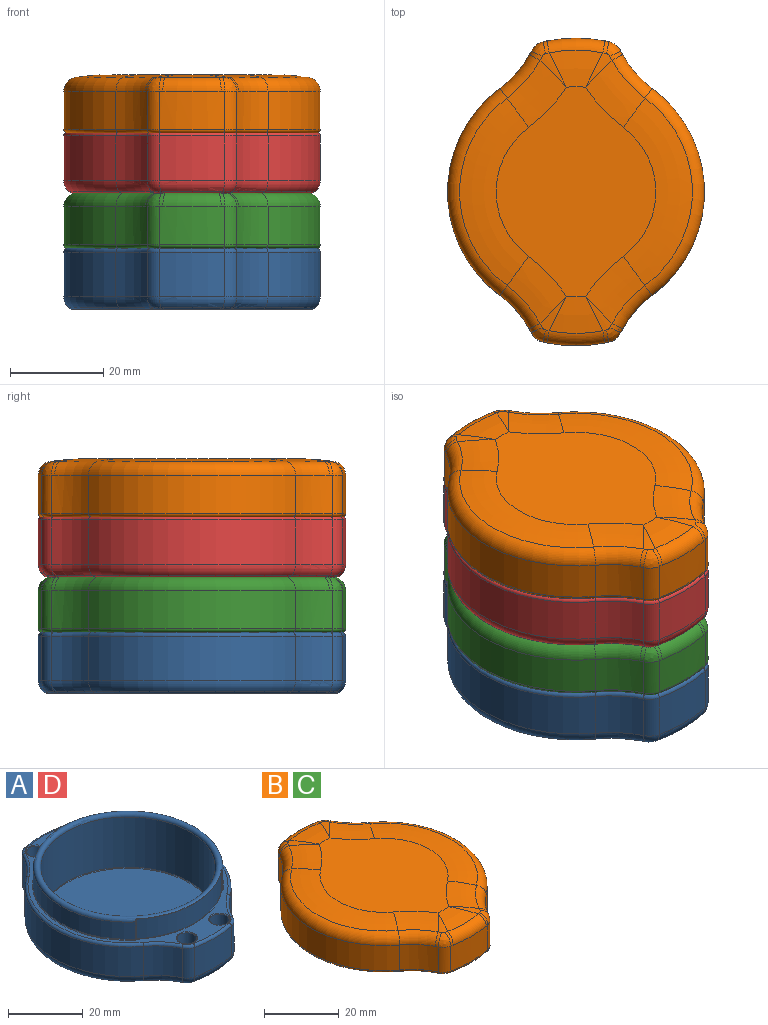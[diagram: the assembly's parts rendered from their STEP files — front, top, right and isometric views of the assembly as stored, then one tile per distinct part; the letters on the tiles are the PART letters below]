
ASSEMBLY  parts=4 mates=1
PART A: 130 faces, bbox 59.6x71.3x20.3 mm
  f0: cylinder r=25.3mm len=38.57mm, axis (0,0,-1), area 245.6mm2, adj f2,f60,f103,f117
  f1: torus R=25.5mm, axis (0,0,-1), area 13.8mm2, adj f3,f6,f114,f129
  f2: torus R=25.5mm, axis (0,0,-1), area 13.8mm2, adj f0,f3,f101,f115
  f3: plane 64.31x53.51mm, normal (0,0,1), area 354.2mm2, adj f1,f2,f39,f40,f41,f42,f43,f44
  f4: cylinder r=27.5mm len=44.33mm, axis (0,0,-1), area 494.9mm2, adj f23,f26,f37,f50
  f5: cylinder r=23.3mm len=46.6mm, axis (0,0,-1), area 2400.9mm2, adj f59,f60
  f6: cylinder r=25.3mm len=38.57mm, axis (0,0,-1), area 245.6mm2, adj f1,f60,f113,f128
  f7: cylinder r=27.5mm len=44.33mm, axis (0,0,-1), area 494.9mm2, adj f24,f25,f28,f39
  f8: plane 46.2x46.2mm, normal (0,0,1), area 1676.4mm2, adj f59
  f9: cylinder r=3.9mm len=9.6mm, axis (0,0,1), area 33.5mm2, adj f10,f25,f32,f42
  f10: cylinder r=32.9mm len=13.89mm, axis (0,0,1), area 134.3mm2, adj f9,f11,f34,f44
  f11: cylinder r=3.9mm len=9.6mm, axis (0,0,1), area 33.5mm2, adj f10,f26,f36,f46
  f12: cylinder r=3.9mm len=9.6mm, axis (0,0,1), area 33.5mm2, adj f13,f23,f33,f47
  f13: cylinder r=32.9mm len=13.89mm, axis (0,0,1), area 134.3mm2, adj f12,f14,f31,f45
  f14: cylinder r=3.9mm len=9.6mm, axis (0,0,1), area 33.5mm2, adj f13,f24,f29,f43
  f15: cylinder r=2.65mm len=11.8mm, axis (0,0,1), area 196.5mm2, adj f57,f58
  f16: plane 4.9x4.9mm, normal (0,0,1), area 18.9mm2, adj f58
  f17: cylinder r=2.65mm len=11.8mm, axis (0,0,1), area 196.5mm2, adj f55,f56
  f18: plane 4.9x4.9mm, normal (0,0,1), area 18.9mm2, adj f56
  f19: cylinder r=2.65mm len=11.8mm, axis (0,0,1), area 196.5mm2, adj f53,f54
  f20: plane 4.9x4.9mm, normal (0,0,1), area 18.9mm2, adj f54
  f21: cylinder r=2.65mm len=11.8mm, axis (0,0,1), area 196.5mm2, adj f51,f52
  f22: plane 4.9x4.9mm, normal (0,0,1), area 18.9mm2, adj f52
  f23: cylinder r=22mm len=9.6mm, axis (0,0,-1), area 100.4mm2, adj f4,f12,f35,f49
  f24: cylinder r=22mm len=9.6mm, axis (0,0,1), area 100.4mm2, adj f7,f14,f27,f41
  f25: cylinder r=22mm len=9.6mm, axis (0,0,-1), area 100.4mm2, adj f7,f9,f30,f40
  f26: cylinder r=22mm len=9.6mm, axis (0,0,1), area 100.4mm2, adj f4,f11,f38,f48
  f27: torus R=25mm, axis (0,0,-1), area 28.2mm2, adj f24,f28,f29,f91,f93
  f28: torus R=24.5mm, axis (0,0,-1), area 134.7mm2, adj f7,f27,f30,f92
  f29: torus R=0.9mm, axis (0,0,-1), area 8.5mm2, adj f14,f27,f31,f89
  f30: torus R=25mm, axis (0,0,-1), area 28.2mm2, adj f25,f28,f32,f88,f90
  f31: torus R=29.9mm, axis (0,0,-1), area 36.6mm2, adj f13,f29,f33,f83,f85,f87
  f32: torus R=0.9mm, axis (0,0,-1), area 8.5mm2, adj f9,f30,f34,f86
  f33: torus R=0.9mm, axis (0,0,-1), area 8.5mm2, adj f12,f31,f35,f81
  f34: torus R=29.9mm, axis (0,0,-1), area 36.6mm2, adj f10,f32,f36,f80,f82,f84
  f35: torus R=25mm, axis (0,0,-1), area 28.2mm2, adj f23,f33,f37,f77,f79
  f36: torus R=0.9mm, axis (0,0,-1), area 8.5mm2, adj f11,f34,f38,f78
  f37: torus R=24.5mm, axis (0,0,-1), area 134.7mm2, adj f4,f35,f38,f75
  f38: torus R=25mm, axis (0,0,-1), area 28.2mm2, adj f26,f36,f37,f74,f76
  f39: torus R=26.7mm, axis (0,0,-1), area 64.1mm2, adj f3,f7,f40,f41
  f40: torus R=22.8mm, axis (0,0,-1), area 13.3mm2, adj f3,f25,f39,f42
  f41: torus R=22.8mm, axis (0,0,-1), area 13.3mm2, adj f3,f24,f39,f43
  f42: torus R=3.1mm, axis (0,0,-1), area 4.1mm2, adj f3,f9,f40,f44
  f43: torus R=3.1mm, axis (0,0,-1), area 4.1mm2, adj f3,f14,f41,f45
  f44: torus R=32.1mm, axis (0,0,-1), area 17.4mm2, adj f3,f10,f42,f46
  f45: torus R=32.1mm, axis (0,0,-1), area 17.4mm2, adj f3,f13,f43,f47
  f46: torus R=3.1mm, axis (0,0,-1), area 4.1mm2, adj f3,f11,f44,f48
  f47: torus R=3.1mm, axis (0,0,-1), area 4.1mm2, adj f3,f12,f45,f49
  f48: torus R=22.8mm, axis (0,0,-1), area 13.3mm2, adj f3,f26,f46,f50
  f49: torus R=22.8mm, axis (0,0,-1), area 13.3mm2, adj f3,f23,f47,f50
  f50: torus R=26.7mm, axis (0,0,-1), area 64.1mm2, adj f3,f4,f48,f49
  f51: torus R=2.85mm, axis (0,0,-1), area 5.4mm2, adj f3,f21
  f52: torus R=2.45mm, axis (0,0,-1), area 5.1mm2, adj f21,f22
  f53: torus R=2.85mm, axis (0,0,-1), area 5.4mm2, adj f3,f19
  f54: torus R=2.45mm, axis (0,0,-1), area 5.1mm2, adj f19,f20
  f55: torus R=2.85mm, axis (0,0,-1), area 5.4mm2, adj f3,f17
  f56: torus R=2.45mm, axis (0,0,-1), area 5.1mm2, adj f17,f18
  f57: torus R=2.85mm, axis (0,0,-1), area 5.4mm2, adj f3,f15
  f58: torus R=2.45mm, axis (0,0,-1), area 5.1mm2, adj f15,f16
  f59: torus R=23.1mm, axis (0,0,-1), area 45.8mm2, adj f5,f8
  f60: torus R=24.3mm, axis (0,0,-1), area 420.2mm2, adj f0,f5,f6,f106,f108,f110,f111,f112
  f61: plane 45.02x34.22mm, normal (0,0,-1), area 1021mm2, adj f62,f63,f64,f67,f68,f71,f72,f73
  f62: torus R=17.11mm, axis (0,0,1), area 327.2mm2, adj f61,f63,f64,f92
  f63: torus R=32.39mm, axis (0,0,-1), area 94mm2, adj f61,f62,f65,f93
  f64: torus R=32.39mm, axis (0,0,-1), area 94mm2, adj f61,f62,f66,f90
  f65: bspline ~9.74x7.58mm, area 12mm2, adj f63,f67,f87,f89,f91
  f66: bspline ~9.74x7.58mm, area 12mm2, adj f64,f68,f84,f86,f88
  f67: torus R=22.51mm, axis (0,0,1), area 63.5mm2, adj f61,f65,f69,f85
  f68: torus R=22.51mm, axis (0,0,1), area 63.5mm2, adj f61,f66,f70,f82
  f69: bspline ~9.74x7.58mm, area 12mm2, adj f67,f71,f79,f81,f83
  f70: bspline ~9.74x7.58mm, area 12mm2, adj f68,f72,f76,f78,f80
  f71: torus R=32.39mm, axis (0,0,-1), area 94mm2, adj f61,f69,f73,f77
  f72: torus R=32.39mm, axis (0,0,-1), area 94mm2, adj f61,f70,f73,f74
  f73: torus R=17.11mm, axis (0,0,1), area 327.2mm2, adj f61,f71,f72,f75
  f74: torus R=23.98mm, axis (0,0,-1), area 12.3mm2, adj f38,f72,f75,f76
  f75: torus R=25.52mm, axis (0,0,1), area 57mm2, adj f37,f73,f74,f77
  f76: bspline ~2.23x1.86mm, area 0.8mm2, adj f38,f70,f74,f78
  f77: torus R=23.98mm, axis (0,0,-1), area 12.3mm2, adj f35,f71,f75,f79
  f78: bspline ~2.64x2.48mm, area 2.4mm2, adj f36,f70,f76,f80
  f79: bspline ~2.23x1.86mm, area 0.8mm2, adj f35,f69,f77,f81
  f80: bspline ~1.64x1.37mm, area 0.7mm2, adj f34,f70,f78,f82
  f81: bspline ~2.64x2.48mm, area 2.4mm2, adj f33,f69,f79,f83
  f82: torus R=30.92mm, axis (0,0,1), area 14.3mm2, adj f34,f68,f80,f84
  f83: bspline ~1.64x1.37mm, area 0.7mm2, adj f31,f69,f81,f85
  f84: bspline ~1.64x1.37mm, area 0.7mm2, adj f34,f66,f82,f86
  f85: torus R=30.92mm, axis (0,0,1), area 14.3mm2, adj f31,f67,f83,f87
  f86: bspline ~2.64x2.48mm, area 2.4mm2, adj f32,f66,f84,f88
  f87: bspline ~1.64x1.37mm, area 0.7mm2, adj f31,f65,f85,f89
  f88: bspline ~1.87x1.68mm, area 0.8mm2, adj f30,f66,f86,f90
  f89: bspline ~2.64x2.48mm, area 2.4mm2, adj f29,f65,f87,f91
  f90: torus R=23.98mm, axis (0,0,-1), area 12.3mm2, adj f30,f64,f88,f92
  f91: bspline ~1.87x1.68mm, area 0.8mm2, adj f27,f65,f89,f93
  f92: torus R=25.52mm, axis (0,0,1), area 57mm2, adj f28,f62,f90,f93
  f93: torus R=23.98mm, axis (0,0,-1), area 12.3mm2, adj f27,f63,f91,f92
  f94: plane 6.11x0.09mm, normal (-0.76,-0.64,0), area 0.6mm2, adj f115,f117,f118,f119,f120
  f95: plane 6.21x0.14mm, normal (0.76,-0.64,0), area 0.6mm2, adj f3,f123,f125,f127,f128,f129
  f96: cylinder r=25mm len=32.06mm, axis (0,0,-1), area 221.7mm2, adj f120,f123,f124,f125
  f97: plane 6.21x0.14mm, normal (0.76,0.64,0), area 0.6mm2, adj f3,f107,f109,f112,f113,f114
  f98: plane 6.11x0.09mm, normal (-0.76,0.64,0), area 0.6mm2, adj f101,f102,f103,f105,f106
  f99: cylinder r=25mm len=32.06mm, axis (0,0,-1), area 221.7mm2, adj f105,f107,f109,f110
  f100: bspline ~0.36x0.18mm, area 0mm2, adj f3,f101,f102
  f101: bspline ~0.34x0.29mm, area 0mm2, adj f2,f98,f100,f103
  f102: cylinder r=0.1mm len=0.15mm, axis (0.64,0.76,0), area 0mm2, adj f3,f98,f100,f104
  f103: cylinder r=0.1mm len=5.6mm, axis (0,0,-1), area 0.9mm2, adj f0,f98,f101,f106
  f104: sphere r=0.1mm, area 0mm2, adj f102,f105,f107
  f105: cylinder r=0.1mm len=6.37mm, axis (0,0,-1), area 1mm2, adj f98,f99,f104,f108
  f106: bspline ~0.67x0.23mm, area 0.1mm2, adj f60,f98,f103,f108
  f107: torus R=25.1mm, axis (0,0,-1), area 5.5mm2, adj f3,f97,f99,f104,f109
  f108: bspline ~0.5x0.36mm, area 0mm2, adj f60,f105,f106,f110
  f109: cylinder r=0.1mm len=6.47mm, axis (0,0,-1), area 1mm2, adj f97,f99,f107,f111
  f110: torus R=24.9mm, axis (0,0,-1), area 2.9mm2, adj f60,f99,f108,f111
  f111: bspline ~0.45x0.35mm, area 0mm2, adj f60,f109,f110,f112
  f112: bspline ~0.67x0.23mm, area 0.1mm2, adj f60,f97,f111,f113
  f113: cylinder r=0.1mm len=5.6mm, axis (0,0,-1), area 0.9mm2, adj f6,f97,f112,f114
  f114: bspline ~0.34x0.29mm, area 0mm2, adj f1,f3,f97,f113
  f115: bspline ~0.34x0.29mm, area 0mm2, adj f2,f94,f116,f117
  f116: bspline ~0.36x0.18mm, area 0mm2, adj f3,f115,f118
  f117: cylinder r=0.1mm len=5.6mm, axis (0,0,-1), area 0.9mm2, adj f0,f94,f115,f119
  f118: cylinder r=0.1mm len=0.15mm, axis (-0.64,0.76,0), area 0mm2, adj f3,f94,f116,f121
  f119: bspline ~0.67x0.23mm, area 0.1mm2, adj f60,f94,f117,f122
  f120: cylinder r=0.1mm len=6.37mm, axis (0,0,-1), area 1mm2, adj f94,f96,f121,f122
  f121: sphere r=0.1mm, area 0mm2, adj f118,f120,f123
  f122: bspline ~0.45x0.35mm, area 0mm2, adj f60,f119,f120,f124
  f123: torus R=25.1mm, axis (0,0,-1), area 5.5mm2, adj f3,f95,f96,f121,f125
  f124: torus R=24.9mm, axis (0,0,-1), area 2.9mm2, adj f60,f96,f122,f126
  f125: cylinder r=0.1mm len=6.47mm, axis (0,0,-1), area 1mm2, adj f95,f96,f123,f126
  f126: bspline ~0.5x0.36mm, area 0mm2, adj f60,f124,f125,f127
  f127: bspline ~0.67x0.23mm, area 0.1mm2, adj f60,f95,f126,f128
  f128: cylinder r=0.1mm len=5.6mm, axis (0,0,-1), area 0.9mm2, adj f6,f95,f127,f129
  f129: bspline ~0.34x0.29mm, area 0mm2, adj f1,f3,f95,f128
PART B: 96 faces, bbox 59.5x71.2x12.5 mm
  f0: plane 64.2x53.4mm, normal (0,0,-1), area 198.8mm2, adj f32,f33,f34,f35,f36,f37,f38,f39
  f1: cylinder r=27.5mm len=44.33mm, axis (0,0,-1), area 421mm2, adj f28,f30,f41,f77
  f2: cylinder r=27.5mm len=44.33mm, axis (0,0,-1), area 421mm2, adj f29,f31,f34,f94
  f3: cylinder r=25.5mm len=49.07mm, axis (0,0,-1), area 482.1mm2, adj f10,f16,f46,f60
  f4: cylinder r=25.5mm len=7.59mm, axis (0,0,-1), area 57.1mm2, adj f6,f15,f16,f50
  f5: cylinder r=25.5mm len=49.07mm, axis (0,0,-1), area 495.3mm2, adj f6,f11,f15,f49
  f6: plane 51x50.8mm, normal (0,0,-1), area 320.6mm2, adj f4,f5,f7,f8,f10,f11,f15,f16
  f7: cylinder r=25.5mm len=7.59mm, axis (0,0,-1), area 57.1mm2, adj f6,f10,f11,f45
  f8: cylinder r=23.3mm len=46.6mm, axis (0,0,-1), area 219.6mm2, adj f6,f61
  f9: plane 37.89x37.89mm, normal (0,0,-1), area 1127.7mm2, adj f75
  f10: cylinder r=3.9mm len=7.5mm, axis (0,0,-1), area 24.9mm2, adj f3,f6,f7,f44,f60
  f11: cylinder r=3.9mm len=7.5mm, axis (0,0,-1), area 24.9mm2, adj f5,f6,f7,f47
  f12: cylinder r=3.9mm len=8.15mm, axis (0,0,-1), area 28.5mm2, adj f13,f31,f33,f91
  f13: cylinder r=32.9mm len=13.89mm, axis (0,0,-1), area 114.3mm2, adj f12,f14,f35,f85,f87,f89
  f14: cylinder r=3.9mm len=8.15mm, axis (0,0,-1), area 28.5mm2, adj f13,f30,f37,f83
  f15: cylinder r=3.9mm len=7.5mm, axis (0,0,-1), area 24.9mm2, adj f4,f5,f6,f51
  f16: cylinder r=3.9mm len=7.5mm, axis (0,0,-1), area 24.9mm2, adj f3,f4,f6,f48,f60
  f17: cylinder r=3.9mm len=8.15mm, axis (0,0,-1), area 28.5mm2, adj f18,f28,f42,f80
  f18: cylinder r=32.9mm len=13.89mm, axis (0,0,-1), area 114.3mm2, adj f17,f19,f40,f82,f84,f86
  f19: cylinder r=3.9mm len=8.15mm, axis (0,0,-1), area 28.5mm2, adj f18,f29,f38,f88
  f20: cylinder r=2.65mm len=10mm, axis (0,0,-1), area 166.5mm2, adj f58,f59
  f21: plane 4.9x4.9mm, normal (0,0,-1), area 18.9mm2, adj f59
  f22: cylinder r=2.65mm len=10mm, axis (0,0,-1), area 166.5mm2, adj f56,f57
  f23: plane 4.9x4.9mm, normal (0,0,-1), area 18.9mm2, adj f57
  f24: cylinder r=2.65mm len=10mm, axis (0,0,-1), area 166.5mm2, adj f54,f55
  f25: plane 4.9x4.9mm, normal (0,0,-1), area 18.9mm2, adj f55
  f26: cylinder r=2.65mm len=10mm, axis (0,0,-1), area 166.5mm2, adj f52,f53
  f27: plane 4.9x4.9mm, normal (0,0,-1), area 18.9mm2, adj f53
  f28: cylinder r=22mm len=8.17mm, axis (0,0,-1), area 85.4mm2, adj f1,f17,f43,f76,f78
  f29: cylinder r=22mm len=8.17mm, axis (0,0,1), area 85.4mm2, adj f2,f19,f36,f90,f92
  f30: cylinder r=22mm len=8.17mm, axis (0,0,1), area 85.4mm2, adj f1,f14,f39,f79,f81
  f31: cylinder r=22mm len=8.17mm, axis (0,0,-1), area 85.4mm2, adj f2,f12,f32,f93,f95
  f32: torus R=22.8mm, axis (0,0,1), area 13.3mm2, adj f0,f31,f33,f34
  f33: torus R=3.1mm, axis (0,0,1), area 4.1mm2, adj f0,f12,f32,f35
  f34: torus R=26.7mm, axis (0,0,1), area 64.1mm2, adj f0,f2,f32,f36
  f35: torus R=32.1mm, axis (0,0,1), area 17.4mm2, adj f0,f13,f33,f37
  f36: torus R=22.8mm, axis (0,0,1), area 13.3mm2, adj f0,f29,f34,f38
  f37: torus R=3.1mm, axis (0,0,1), area 4.1mm2, adj f0,f14,f35,f39
  f38: torus R=3.1mm, axis (0,0,1), area 4.1mm2, adj f0,f19,f36,f40
  f39: torus R=22.8mm, axis (0,0,1), area 13.3mm2, adj f0,f30,f37,f41
  f40: torus R=32.1mm, axis (0,0,1), area 17.4mm2, adj f0,f18,f38,f42
  f41: torus R=26.7mm, axis (0,0,1), area 64.1mm2, adj f0,f1,f39,f43
  f42: torus R=3.1mm, axis (0,0,1), area 4.1mm2, adj f0,f17,f40,f43
  f43: torus R=22.8mm, axis (0,0,1), area 13.3mm2, adj f0,f28,f41,f42
  f44: torus R=3.1mm, axis (0,0,1), area 4.1mm2, adj f0,f10,f45,f46
  f45: torus R=26.3mm, axis (0,0,1), area 9.9mm2, adj f0,f7,f44,f47
  f46: torus R=26.3mm, axis (0,0,1), area 84.2mm2, adj f0,f3,f44,f48
  f47: torus R=3.1mm, axis (0,0,1), area 4.1mm2, adj f0,f11,f45,f49
  f48: torus R=3.1mm, axis (0,0,1), area 4.1mm2, adj f0,f16,f46,f50
  f49: torus R=26.3mm, axis (0,0,1), area 84.2mm2, adj f0,f5,f47,f51
  f50: torus R=26.3mm, axis (0,0,1), area 9.9mm2, adj f0,f4,f48,f51
  f51: torus R=3.1mm, axis (0,0,1), area 4.1mm2, adj f0,f15,f49,f50
  f52: torus R=2.85mm, axis (0,0,1), area 5.4mm2, adj f0,f26
  f53: torus R=2.45mm, axis (0,0,-1), area 5.1mm2, adj f26,f27
  f54: torus R=2.85mm, axis (0,0,1), area 5.4mm2, adj f0,f24
  f55: torus R=2.45mm, axis (0,0,-1), area 5.1mm2, adj f24,f25
  f56: torus R=2.85mm, axis (0,0,1), area 5.4mm2, adj f0,f22
  f57: torus R=2.45mm, axis (0,0,-1), area 5.1mm2, adj f22,f23
  f58: torus R=2.85mm, axis (0,0,1), area 5.4mm2, adj f0,f20
  f59: torus R=2.45mm, axis (0,0,-1), area 5.1mm2, adj f20,f21
  f60: torus R=25.3mm, axis (0,0,-1), area 20.8mm2, adj f3,f6,f10,f16
  f61: torus R=22.3mm, axis (0,0,1), area 401.4mm2, adj f8,f75
  f62: plane 45.02x34.22mm, normal (0,0,1), area 1021mm2, adj f63,f64,f65,f68,f69,f72,f73,f74
  f63: torus R=17.11mm, axis (0,0,1), area 309.4mm2, adj f62,f64,f65,f94
  f64: torus R=32.39mm, axis (0,0,-1), area 89.8mm2, adj f62,f63,f66,f92
  f65: torus R=32.39mm, axis (0,0,-1), area 89.8mm2, adj f62,f63,f67,f95
  f66: bspline ~9.74x7.58mm, area 11mm2, adj f64,f68,f86,f88,f90
  f67: bspline ~9.74x7.58mm, area 11mm2, adj f65,f69,f89,f91,f93
  f68: torus R=22.51mm, axis (0,0,1), area 59.3mm2, adj f62,f66,f70,f84
  f69: torus R=22.51mm, axis (0,0,1), area 59.3mm2, adj f62,f67,f71,f87
  f70: bspline ~9.74x7.58mm, area 11mm2, adj f68,f72,f78,f80,f82
  f71: bspline ~9.74x7.58mm, area 11mm2, adj f69,f73,f81,f83,f85
  f72: torus R=32.39mm, axis (0,0,-1), area 89.8mm2, adj f62,f70,f74,f76
  f73: torus R=32.39mm, axis (0,0,-1), area 89.8mm2, adj f62,f71,f74,f79
  f74: torus R=17.11mm, axis (0,0,1), area 309.4mm2, adj f62,f72,f73,f77
  f75: torus R=18.95mm, axis (0,0,-1), area 409.3mm2, adj f9,f61
  f76: torus R=25mm, axis (0,0,1), area 43.1mm2, adj f28,f72,f77,f78
  f77: torus R=24.5mm, axis (0,0,1), area 213.3mm2, adj f1,f74,f76,f79
  f78: bspline ~3.2x3.03mm, area 3.8mm2, adj f28,f70,f76,f80
  f79: torus R=25mm, axis (0,0,1), area 43.1mm2, adj f30,f73,f77,f81
  f80: bspline ~3.37x3.3mm, area 10.8mm2, adj f17,f70,f78,f82
  f81: bspline ~3.13x3.01mm, area 3.8mm2, adj f30,f71,f79,f83
  f82: bspline ~3.09x3.02mm, area 3.4mm2, adj f18,f70,f80,f84
  f83: bspline ~3.44x3.33mm, area 10.8mm2, adj f14,f71,f81,f85
  f84: torus R=29.9mm, axis (0,0,-1), area 52.2mm2, adj f18,f68,f82,f86
  f85: bspline ~3.01x2.9mm, area 3.4mm2, adj f13,f71,f83,f87
  f86: bspline ~3.01x2.9mm, area 3.4mm2, adj f18,f66,f84,f88
  f87: torus R=29.9mm, axis (0,0,-1), area 52.2mm2, adj f13,f69,f85,f89
  f88: bspline ~3.44x3.33mm, area 10.8mm2, adj f19,f66,f86,f90
  f89: bspline ~3.03x2.98mm, area 3.3mm2, adj f13,f67,f87,f91
  f90: bspline ~3.13x3.01mm, area 3.8mm2, adj f29,f66,f88,f92
  f91: bspline ~3.37x3.3mm, area 10.8mm2, adj f12,f67,f89,f93
  f92: torus R=25mm, axis (0,0,1), area 43.1mm2, adj f29,f64,f90,f94
  f93: bspline ~3.2x3.03mm, area 3.8mm2, adj f31,f67,f91,f95
  f94: torus R=24.5mm, axis (0,0,1), area 213.3mm2, adj f2,f63,f92,f95
  f95: torus R=25mm, axis (0,0,1), area 43.1mm2, adj f31,f65,f93,f94
PART C: same geometry as B
PART D: same geometry as A
PLACE A at identity
PLACE B t=(0,0,24.7)mm
PLACE C at identity
PLACE D t=(0,0,24.9)mm
MATE revolute B.f77 <-> D.f28  axis (0,0,-1) through (0,0,38.1)mm
